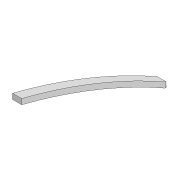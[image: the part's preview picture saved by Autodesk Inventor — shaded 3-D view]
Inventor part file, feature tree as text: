
AUTODESK INVENTOR PART (.ipt)
format: ipt  version: 2022 (Build 260153000, 153)  size: 127,488 bytes
history: native  units: mm
features: extrude x3, sketch x3, projected_geometry x2, fillet x1
ambient origin geometry x8: Origin, YZ Plane, XZ Plane, XY Plane, X Axis, Y Axis, Z Axis, Center Point
bodies: Solid1 (feature_tree)
feature tree (9):
  extrude  "Extrusion1"  Depth=10.0mm
  extrude  "Extrusion2"  Depth=40.0mm
  fillet  "Fillet1"  Radius=140.0mm
  extrude  "Extrusion3"  Depth=2.0mm TaperAngle=0.0deg
  sketch  "Sketch1"  dims[d0=180.0mm d1=10.0mm]
  sketch  "Sketch2"  dims[d2=3.3mm d3=40.0mm d5=140.0mm]
  projected_geometry  "Projected Loop1"
  projected_geometry  "Projected Loop2"
  sketch  "Sketch3"  dims[d6=3.3mm d7=6.0mm d8=0.0mm d9=6.0mm d10=498.004mm d11=90.0mm d12=10.0mm d13=0.0mm d14=2.0mm d15=100.0mm d16=0.0mm]
